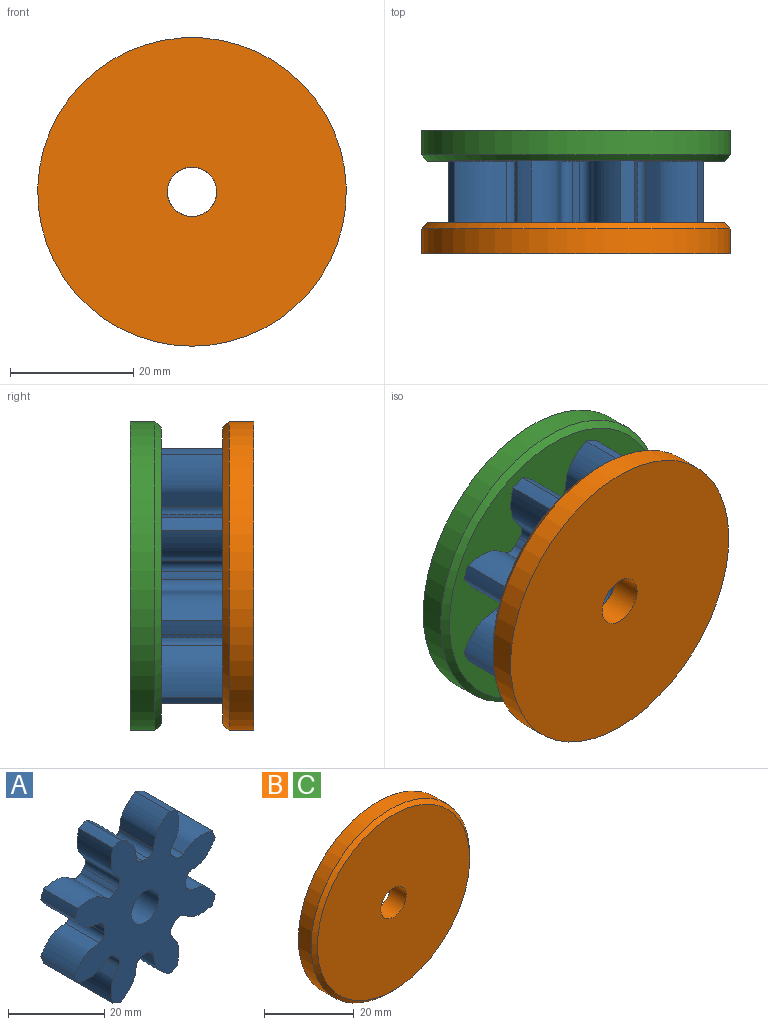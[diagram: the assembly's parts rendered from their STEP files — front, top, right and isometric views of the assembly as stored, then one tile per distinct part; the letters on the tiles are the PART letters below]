
ASSEMBLY  parts=3 mates=2
PART A: 51 faces, bbox 41.5x10x41.5 mm
  f0: cylinder r=21.88mm len=10mm, axis (0,1,0), area 23.6mm2, adj f7,f10,f41,f48
  f1: cylinder r=21.88mm len=10mm, axis (0,1,0), area 23.6mm2, adj f7,f10,f36,f43
  f2: cylinder r=21.88mm len=10mm, axis (0,1,0), area 23.6mm2, adj f7,f10,f31,f38
  f3: cylinder r=21.88mm len=10mm, axis (0,1,0), area 23.6mm2, adj f7,f10,f26,f33
  f4: cylinder r=21.88mm len=10mm, axis (0,1,0), area 23.6mm2, adj f7,f10,f21,f28
  f5: cylinder r=21.88mm len=10mm, axis (0,1,0), area 23.6mm2, adj f7,f10,f16,f23
  f6: cylinder r=21.88mm len=10mm, axis (0,1,0), area 23.6mm2, adj f7,f10,f11,f18
  f7: plane 41.47x41.47mm, normal (0,-1,0), area 862.8mm2, adj f0,f1,f2,f3,f4,f5,f6,f8
  f8: cylinder r=4mm len=10mm, axis (0,1,0), area 251.3mm2, adj f7,f10
  f9: cylinder r=21.88mm len=10mm, axis (0,1,0), area 23.6mm2, adj f7,f10,f13,f46
  f10: plane 41.47x41.47mm, normal (0,1,0), area 862.8mm2, adj f0,f1,f2,f3,f4,f5,f6,f8
  f11: extruded ~10x7.17mm, area 90.3mm2, adj f6,f7,f10,f14
  f12: cylinder r=12.03mm len=10mm, axis (0,1,0), area 12.8mm2, adj f7,f10,f14,f15
  f13: extruded ~10x7.17mm, area 90.3mm2, adj f7,f9,f10,f15
  f14: cylinder r=1.76mm len=10mm, axis (0,1,0), area 25.5mm2, adj f7,f10,f11,f12
  f15: cylinder r=1.76mm len=10mm, axis (0,1,0), area 25.5mm2, adj f7,f10,f12,f13
  f16: extruded ~10x8.47mm, area 90.3mm2, adj f5,f7,f10,f19
  f17: cylinder r=12.03mm len=10mm, axis (0,1,0), area 12.8mm2, adj f7,f10,f19,f20
  f18: extruded ~10x8.47mm, area 90.3mm2, adj f6,f7,f10,f20
  f19: cylinder r=1.76mm len=10mm, axis (0,1,0), area 25.5mm2, adj f7,f10,f16,f17
  f20: cylinder r=1.76mm len=10mm, axis (0,1,0), area 25.5mm2, adj f7,f10,f17,f18
  f21: extruded ~10x7.17mm, area 90.3mm2, adj f4,f7,f10,f24
  f22: cylinder r=12.03mm len=10mm, axis (0,1,0), area 12.8mm2, adj f7,f10,f24,f25
  f23: extruded ~10x7.17mm, area 90.3mm2, adj f5,f7,f10,f25
  f24: cylinder r=1.76mm len=10mm, axis (0,1,0), area 25.5mm2, adj f7,f10,f21,f22
  f25: cylinder r=1.76mm len=10mm, axis (0,1,0), area 25.5mm2, adj f7,f10,f22,f23
  f26: extruded ~10x8.47mm, area 90.3mm2, adj f3,f7,f10,f29
  f27: cylinder r=12.03mm len=10mm, axis (0,1,0), area 12.8mm2, adj f7,f10,f29,f30
  f28: extruded ~10x8.47mm, area 90.3mm2, adj f4,f7,f10,f30
  f29: cylinder r=1.76mm len=10mm, axis (0,1,0), area 25.5mm2, adj f7,f10,f26,f27
  f30: cylinder r=1.76mm len=10mm, axis (0,1,0), area 25.5mm2, adj f7,f10,f27,f28
  f31: extruded ~10x7.17mm, area 90.3mm2, adj f2,f7,f10,f34
  f32: cylinder r=12.03mm len=10mm, axis (0,1,0), area 12.8mm2, adj f7,f10,f34,f35
  f33: extruded ~10x7.17mm, area 90.3mm2, adj f3,f7,f10,f35
  f34: cylinder r=1.76mm len=10mm, axis (0,1,0), area 25.5mm2, adj f7,f10,f31,f32
  f35: cylinder r=1.76mm len=10mm, axis (0,1,0), area 25.5mm2, adj f7,f10,f32,f33
  f36: extruded ~10x8.47mm, area 90.3mm2, adj f1,f7,f10,f39
  f37: cylinder r=12.03mm len=10mm, axis (0,1,0), area 12.8mm2, adj f7,f10,f39,f40
  f38: extruded ~10x8.47mm, area 90.3mm2, adj f2,f7,f10,f40
  f39: cylinder r=1.76mm len=10mm, axis (0,1,0), area 25.5mm2, adj f7,f10,f36,f37
  f40: cylinder r=1.76mm len=10mm, axis (0,1,0), area 25.5mm2, adj f7,f10,f37,f38
  f41: extruded ~10x7.17mm, area 90.3mm2, adj f0,f7,f10,f44
  f42: cylinder r=12.03mm len=10mm, axis (0,1,0), area 12.8mm2, adj f7,f10,f44,f45
  f43: extruded ~10x7.17mm, area 90.3mm2, adj f1,f7,f10,f45
  f44: cylinder r=1.76mm len=10mm, axis (0,1,0), area 25.5mm2, adj f7,f10,f41,f42
  f45: cylinder r=1.76mm len=10mm, axis (0,1,0), area 25.5mm2, adj f7,f10,f42,f43
  f46: extruded ~10x8.47mm, area 90.3mm2, adj f7,f9,f10,f49
  f47: cylinder r=12.03mm len=10mm, axis (0,1,0), area 12.8mm2, adj f7,f10,f49,f50
  f48: extruded ~10x8.47mm, area 90.3mm2, adj f0,f7,f10,f50
  f49: cylinder r=1.76mm len=10mm, axis (0,1,0), area 25.5mm2, adj f7,f10,f46,f47
  f50: cylinder r=1.76mm len=10mm, axis (0,1,0), area 25.5mm2, adj f7,f10,f47,f48
PART B: 5 faces, bbox 50x5x50 mm
  f0: cylinder r=4mm len=8mm, axis (0,1,0), area 125.7mm2, adj f2,f3
  f1: cylinder r=25mm len=50mm, axis (0,1,0), area 628.3mm2, adj f3,f4
  f2: plane 48x48mm, normal (0,-1,0), area 1759.3mm2, adj f0,f4
  f3: plane 50x50mm, normal (0,1,0), area 1913.2mm2, adj f0,f1
  f4: cone r=24mm half-angle=45deg, axis (0,1,0), area 217.7mm2, adj f1,f2
PART C: same geometry as B
PLACE A t=(0,-5,0)mm
PLACE B rot(axis=(0,0,1),180deg) t=(0,-20,0)mm
PLACE C at identity
MATE fastened A.f0 <-> C.f0  axis (0,1,0) through (0,-5,0)mm
MATE fastened A.f0 <-> B.f0  axis (0,-1,0) through (0,-15,0)mm
